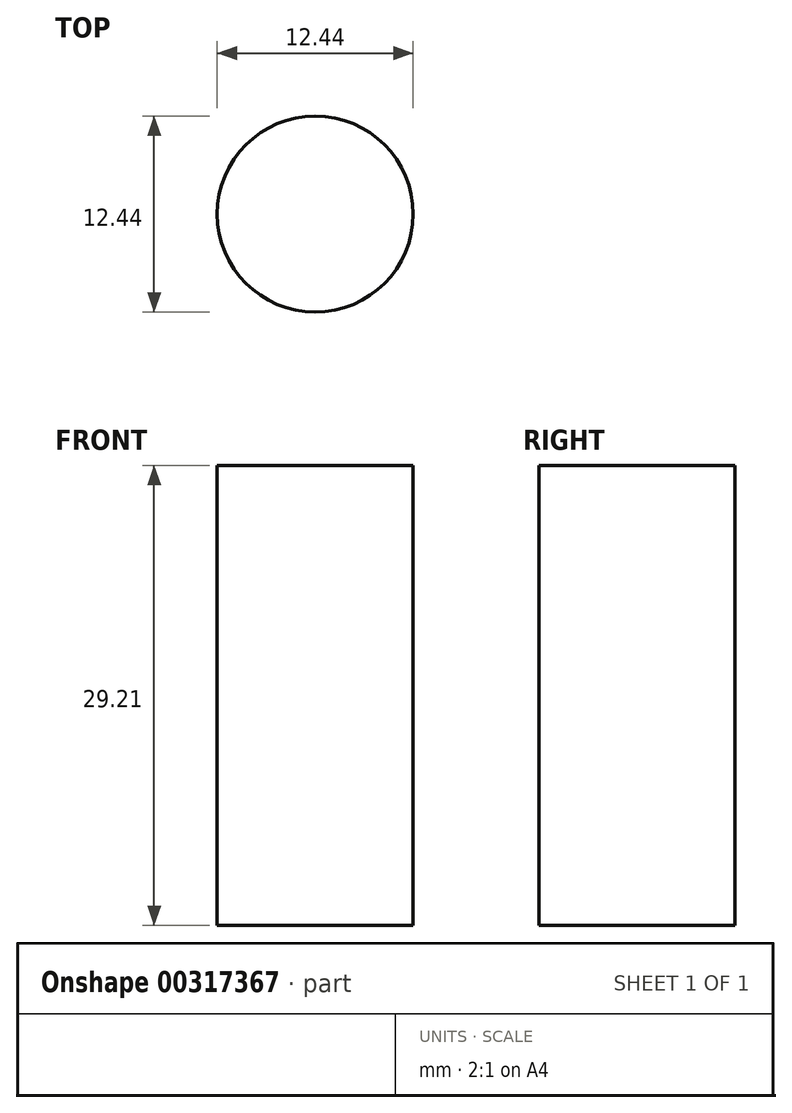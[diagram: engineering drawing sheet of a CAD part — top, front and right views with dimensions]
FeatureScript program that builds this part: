
annotation { "Feature Type Name" : "Feature", "Feature Type Description" : "" }
export const myFeature = defineFeature(function(context is Context, id is Id, definition is map)
    precondition{}
    {
        {
            var Q0;
            Q0=qCreatedBy(makeId("Top.planeOp"),FACE);
            var sketch = newSketch(context, id + "F0", { "sketchPlane" : qUnion([Q0])});
            skCircle(sketch, "E0", {"center": v(0, 0) * mm, "radius": 6.22 * mm});
            skSolve(sketch);
        }
        {
            var Q0;
            Q0=makeQuery(id+"F0.imprint","IMPRINT",FACE,{"disambiguationData":[TD([[makeQuery(id+"F0.imprint","IMPRINT",EDGE,{"derivedFrom":sQuery(id+"F0.wireOp",EDGE,"E0")}),1.0]])]});
            extrude(context, id + "F1", {"entities" : qUnion([Q0]), "depth" : 29.2 * mm});
        }
    });
